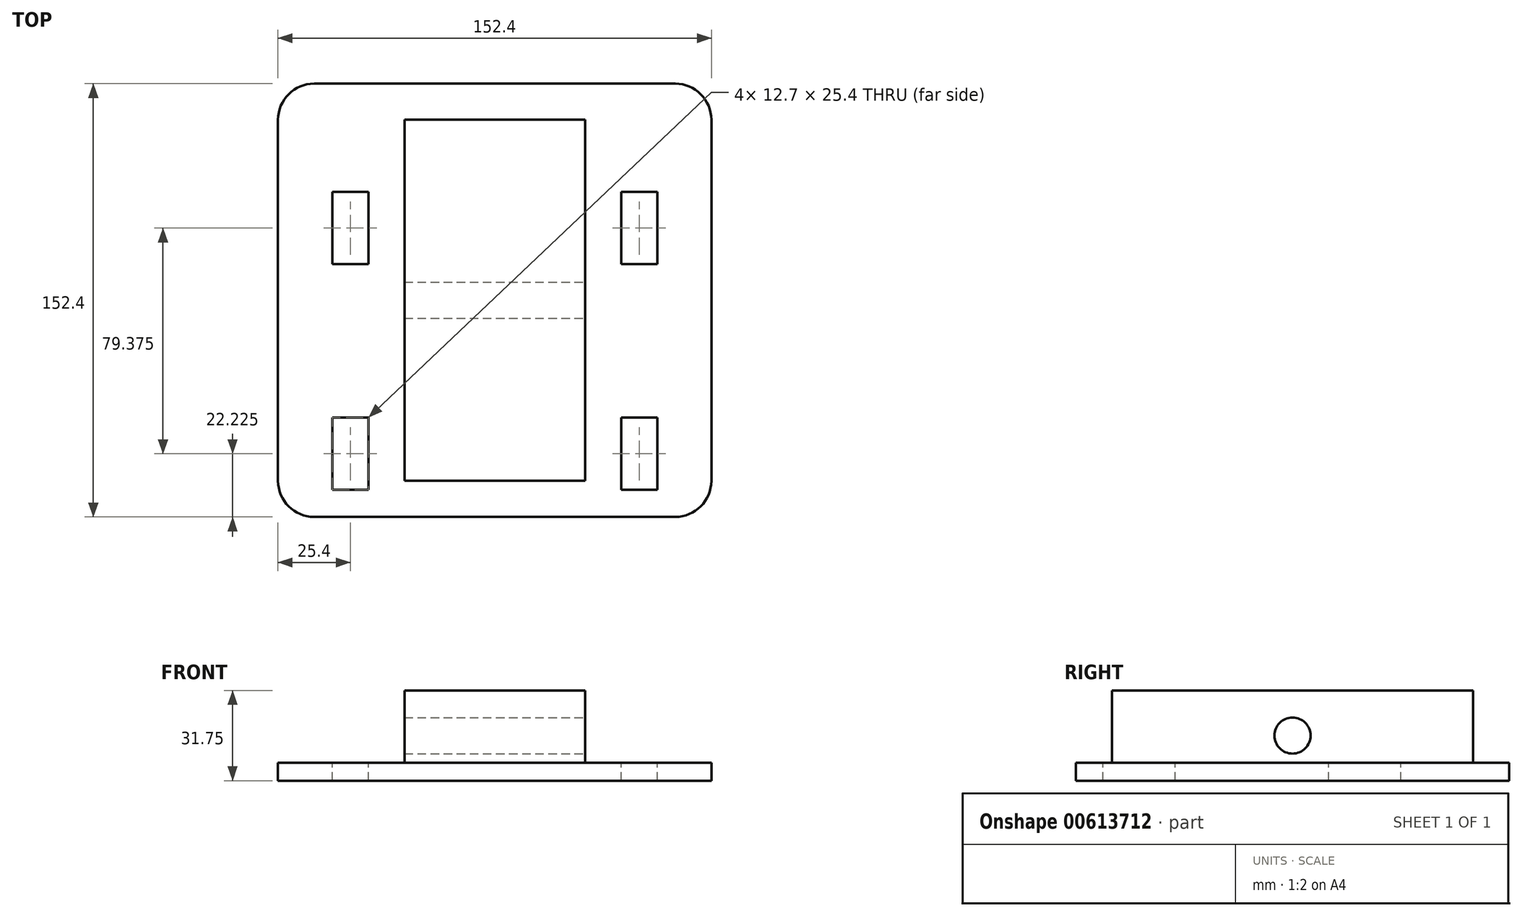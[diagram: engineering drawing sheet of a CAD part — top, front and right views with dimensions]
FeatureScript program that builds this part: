
annotation { "Feature Type Name" : "Feature", "Feature Type Description" : "" }
export const myFeature = defineFeature(function(context is Context, id is Id, definition is map)
    precondition{}
    {
        {
            var Q0;
            Q0=qCreatedBy(makeId("Top.planeOp"),FACE);
            var sketch = newSketch(context, id + "F0", { "sketchPlane" : qUnion([Q0])});
            skLineSegment(sketch, "E0.bottom", {"start": v(-63.5, 76.2) * mm, "end": v(63.5, 76.2) * mm});
            skLineSegment(sketch, "E0.top", {"start": v(-63.5, -76.2) * mm, "end": v(63.5, -76.2) * mm});
            skLineSegment(sketch, "E0.left", {"start": v(-76.2, 63.5) * mm, "end": v(-76.2, -63.5) * mm});
            skLineSegment(sketch, "E0.right", {"start": v(76.2, 63.5) * mm, "end": v(76.2, -63.5) * mm});
            skPoint(sketch, "E1.visualSharp", {"position": v(-76.2, 76.2) * mm});
            skArc(sketch, "E1.filletArc", {"start": v(-63.5, 76.2) * mm, "mid": v(-72.48, 72.48) * mm, "end": v(-76.2, 63.5) * mm});
            skPoint(sketch, "E2.visualSharp", {"position": v(-76.2, -76.2) * mm});
            skArc(sketch, "E2.filletArc", {"start": v(-76.2, -63.5) * mm, "mid": v(-72.48, -72.48) * mm, "end": v(-63.5, -76.2) * mm});
            skPoint(sketch, "E3.visualSharp", {"position": v(76.2, 76.2) * mm});
            skArc(sketch, "E3.filletArc", {"start": v(76.2, 63.5) * mm, "mid": v(72.48, 72.48) * mm, "end": v(63.5, 76.2) * mm});
            skPoint(sketch, "E4.visualSharp", {"position": v(76.2, -76.2) * mm});
            skArc(sketch, "E4.filletArc", {"start": v(63.5, -76.2) * mm, "mid": v(72.48, -72.48) * mm, "end": v(76.2, -63.5) * mm});
            skLineSegment(sketch, "E5.bottom", {"start": v(-57.15, 69.85) * mm, "end": v(57.15, 69.85) * mm});
            skLineSegment(sketch, "E5.top", {"start": v(-57.15, -69.85) * mm, "end": v(57.15, -69.85) * mm});
            skLineSegment(sketch, "E5.left", {"start": v(-69.85, 57.15) * mm, "end": v(-69.85, -57.15) * mm});
            skLineSegment(sketch, "E5.right", {"start": v(69.85, 57.15) * mm, "end": v(69.85, -57.15) * mm});
            skPoint(sketch, "E6.visualSharp", {"position": v(-69.85, 69.85) * mm});
            skArc(sketch, "E6.filletArc", {"start": v(-57.15, 69.85) * mm, "mid": v(-66.13, 66.13) * mm, "end": v(-69.85, 57.15) * mm});
            skPoint(sketch, "E7.visualSharp", {"position": v(-69.85, -69.85) * mm});
            skArc(sketch, "E7.filletArc", {"start": v(-69.85, -57.15) * mm, "mid": v(-66.13, -66.13) * mm, "end": v(-57.15, -69.85) * mm});
            skPoint(sketch, "E8.visualSharp", {"position": v(69.85, 69.85) * mm});
            skArc(sketch, "E8.filletArc", {"start": v(69.85, 57.15) * mm, "mid": v(66.13, 66.13) * mm, "end": v(57.15, 69.85) * mm});
            skPoint(sketch, "E9.visualSharp", {"position": v(69.85, -69.85) * mm});
            skArc(sketch, "E9.filletArc", {"start": v(57.15, -69.85) * mm, "mid": v(66.13, -66.13) * mm, "end": v(69.85, -57.15) * mm});
            skCircle(sketch, "E10", {"center": v(0, 0) * mm, "radius": 69.85 * mm});
            skSolve(sketch);
        }
        {
            var Q0;
            Q0=sQuery(id+"F0.wireOp",EDGE,"E0.bottom");
            var Q1;
            Q1=sQuery(id+"F0.wireOp",EDGE,"E1.filletArc");
            var Q2;
            Q2=sQuery(id+"F0.wireOp",EDGE,"E0.left");
            var Q3;
            Q3=sQuery(id+"F0.wireOp",EDGE,"E2.filletArc");
            var Q4;
            Q4=sQuery(id+"F0.wireOp",EDGE,"E0.top");
            var Q5;
            Q5=sQuery(id+"F0.wireOp",EDGE,"E4.filletArc");
            var Q6;
            Q6=sQuery(id+"F0.wireOp",EDGE,"E0.right");
            var Q7;
            Q7=sQuery(id+"F0.wireOp",EDGE,"E3.filletArc");
            var Q8;
            Q8=sQuery(id+"F0.wireOp",EDGE,"E5.bottom");
            var Q9;
            Q9=sQuery(id+"F0.wireOp",EDGE,"E6.filletArc");
            var Q10;
            Q10=sQuery(id+"F0.wireOp",EDGE,"E5.left");
            var Q11;
            Q11=sQuery(id+"F0.wireOp",EDGE,"E5.top");
            var Q12;
            Q12=sQuery(id+"F0.wireOp",EDGE,"E7.filletArc");
            var Q13;
            Q13=sQuery(id+"F0.wireOp",EDGE,"E5.right");
            var Q14;
            Q14=sQuery(id+"F0.wireOp",EDGE,"E8.filletArc");
            var Q15;
            Q15=sQuery(id+"F0.wireOp",EDGE,"E9.filletArc");
            extrude(context, id + "F1", {"bodyType" : ToolBodyType.SURFACE, "surfaceEntities" : qUnion([Q0, Q1, Q2, Q3, Q4, Q5, Q6, Q7, Q8, Q9, Q10, Q11, Q12, Q13, Q14, Q15]), "oppositeDirection" : true, "depth" : 50.8 * mm, "offsetDistance" : 25.4 * mm});
        }
        {
            var Q0;
            {var subQ0=sQuery(id+"F0.wireOp",EDGE,"E8.filletArc");Q0=makeQuery(id+"F0.imprint","IMPRINT",FACE,{"disambiguationData":[TD([[makeQuery(id+"F0.imprint","IMPRINT",EDGE,{"derivedFrom":subQ0}),1.0]])]});}
            var Q1;
            {var subQ0=sQuery(id+"F0.wireOp",EDGE,"E10");var subQ1=makeQuery(id+"F0.imprint","INTERSECT",VERTEX,{"derivedFrom":[sQuery(id+"F0.wireOp",EDGE,"E5.bottom"),subQ0]});Q1=makeQuery(id+"F0.imprint","IMPRINT",FACE,{"disambiguationData":[TD([[makeQuery(id+"F0.imprint","IMPRINT",EDGE,{"disambiguationData":[TD([[subQ1,1.0]])],"derivedFrom":subQ0}),1.0]])]});}
            var Q2;
            {var subQ0=sQuery(id+"F0.wireOp",EDGE,"E6.filletArc");Q2=makeQuery(id+"F0.imprint","IMPRINT",FACE,{"disambiguationData":[TD([[makeQuery(id+"F0.imprint","IMPRINT",EDGE,{"derivedFrom":subQ0}),1.0]])]});}
            var Q3;
            {var subQ0=sQuery(id+"F0.wireOp",EDGE,"E9.filletArc");Q3=makeQuery(id+"F0.imprint","IMPRINT",FACE,{"disambiguationData":[TD([[makeQuery(id+"F0.imprint","IMPRINT",EDGE,{"derivedFrom":subQ0}),1.0]])]});}
            var Q4;
            {var subQ0=sQuery(id+"F0.wireOp",EDGE,"E7.filletArc");Q4=makeQuery(id+"F0.imprint","IMPRINT",FACE,{"disambiguationData":[TD([[makeQuery(id+"F0.imprint","IMPRINT",EDGE,{"derivedFrom":subQ0}),1.0]])]});}
            var Q5;
            Q5=makeQuery(id+"F0.imprint","IMPRINT",FACE,{"disambiguationData":[TD([[makeQuery(id+"F0.imprint","IMPRINT",EDGE,{"derivedFrom":sQuery(id+"F0.wireOp",EDGE,"E0.bottom")}),-1.0]])]});
            extrude(context, id + "F2", {"entities" : qUnion([Q0, Q1, Q2, Q3, Q4, Q5]), "depth" : 6.35 * mm, "offsetDistance" : 25.4 * mm});
        }
        {
            var Q0;
            Q0=makeQuery(id+"F2.opExtrude","CAP_FACE",FACE,{"disambiguationData":[OSD([sQuery(id+"F0.wireOp",EDGE,"E0.bottom"),sQuery(id+"F0.wireOp",EDGE,"E0.top"),sQuery(id+"F0.wireOp",EDGE,"E0.left"),sQuery(id+"F0.wireOp",EDGE,"E0.right"),sQuery(id+"F0.wireOp",EDGE,"E1.filletArc"),sQuery(id+"F0.wireOp",EDGE,"E2.filletArc"),sQuery(id+"F0.wireOp",EDGE,"E3.filletArc"),sQuery(id+"F0.wireOp",EDGE,"E4.filletArc")])],"isStart":false});
            var sketch = newSketch(context, id + "F3", { "sketchPlane" : qUnion([Q0])});
            skLineSegment(sketch, "E11.bottom", {"start": v(-31.75, 63.5) * mm, "end": v(31.75, 63.5) * mm});
            skLineSegment(sketch, "E11.top", {"start": v(-31.75, -63.5) * mm, "end": v(31.75, -63.5) * mm});
            skLineSegment(sketch, "E11.left", {"start": v(-31.75, 63.5) * mm, "end": v(-31.75, -63.5) * mm});
            skLineSegment(sketch, "E11.right", {"start": v(31.75, 63.5) * mm, "end": v(31.75, -63.5) * mm});
            skSolve(sketch);
        }
        {
            var Q0;
            Q0=makeQuery(id+"F3.imprint","IMPRINT",FACE,{"disambiguationData":[TD([[makeQuery(id+"F3.imprint","IMPRINT",EDGE,{"derivedFrom":sQuery(id+"F3.wireOp",EDGE,"E11.bottom")}),-1.0]])]});
            extrude(context, id + "F4", {"entities" : qUnion([Q0]), "operationType" : NewBodyOperationType.ADD, "depth" : 25.4 * mm, "offsetDistance" : 25.4 * mm});
        }
        {
            var Q0;
            Q0=makeQuery(id+"F4.opExtrude","SWEPT_FACE",FACE,{"disambiguationData":[OSD([sQuery(id+"F3.wireOp",EDGE,"E11.right")])]});
            var sketch = newSketch(context, id + "F5", { "sketchPlane" : qUnion([Q0])});
            skCircle(sketch, "E12", {"center": v(0, 15.88) * mm, "radius": 6.35 * mm});
            skSolve(sketch);
        }
        {
            var Q0;
            Q0=makeQuery(id+"F5.imprint","IMPRINT",FACE,{"disambiguationData":[TD([[makeQuery(id+"F5.imprint","IMPRINT",EDGE,{"derivedFrom":sQuery(id+"F5.wireOp",EDGE,"E12")}),1.0]])]});
            extrude(context, id + "F6", {"entities" : qUnion([Q0]), "operationType" : NewBodyOperationType.REMOVE, "oppositeDirection" : true, "depth" : 63.5 * mm, "offsetDistance" : 25.4 * mm});
        }
        {
            var Q0;
            Q0=makeQuery(id+"F2.opExtrude","CAP_FACE",FACE,{"disambiguationData":[OSD([sQuery(id+"F0.wireOp",EDGE,"E0.bottom"),sQuery(id+"F0.wireOp",EDGE,"E0.top"),sQuery(id+"F0.wireOp",EDGE,"E0.left"),sQuery(id+"F0.wireOp",EDGE,"E0.right"),sQuery(id+"F0.wireOp",EDGE,"E1.filletArc"),sQuery(id+"F0.wireOp",EDGE,"E2.filletArc"),sQuery(id+"F0.wireOp",EDGE,"E3.filletArc"),sQuery(id+"F0.wireOp",EDGE,"E4.filletArc")])],"isStart":false});
            var sketch = newSketch(context, id + "F7", { "sketchPlane" : qUnion([Q0])});
            skLineSegment(sketch, "E13.bottom", {"start": v(-57.15, -41.28) * mm, "end": v(-44.45, -41.28) * mm});
            skLineSegment(sketch, "E13.top", {"start": v(-57.15, -66.68) * mm, "end": v(-44.45, -66.68) * mm});
            skLineSegment(sketch, "E13.left", {"start": v(-57.15, -41.28) * mm, "end": v(-57.15, -66.68) * mm});
            skLineSegment(sketch, "E13.right", {"start": v(-44.45, -41.28) * mm, "end": v(-44.45, -66.68) * mm});
            skLineSegment(sketch, "E14.bottom", {"start": v(44.45, -66.68) * mm, "end": v(57.15, -66.68) * mm});
            skLineSegment(sketch, "E14.top", {"start": v(44.45, -41.28) * mm, "end": v(57.15, -41.28) * mm});
            skLineSegment(sketch, "E14.left", {"start": v(44.45, -66.67) * mm, "end": v(44.45, -41.27) * mm});
            skLineSegment(sketch, "E14.right", {"start": v(57.15, -66.67) * mm, "end": v(57.15, -41.27) * mm});
            skLineSegment(sketch, "E15.bottom", {"start": v(-44.45, 12.7) * mm, "end": v(-57.15, 12.7) * mm});
            skLineSegment(sketch, "E15.top", {"start": v(-44.45, 38.1) * mm, "end": v(-57.15, 38.1) * mm});
            skLineSegment(sketch, "E15.left", {"start": v(-44.45, 12.7) * mm, "end": v(-44.45, 38.1) * mm});
            skLineSegment(sketch, "E15.right", {"start": v(-57.15, 12.7) * mm, "end": v(-57.15, 38.1) * mm});
            skLineSegment(sketch, "E16.bottom", {"start": v(44.45, 12.7) * mm, "end": v(57.15, 12.7) * mm});
            skLineSegment(sketch, "E16.top", {"start": v(44.45, 38.1) * mm, "end": v(57.15, 38.1) * mm});
            skLineSegment(sketch, "E16.left", {"start": v(44.45, 12.7) * mm, "end": v(44.45, 38.1) * mm});
            skLineSegment(sketch, "E16.right", {"start": v(57.15, 12.7) * mm, "end": v(57.15, 38.1) * mm});
            skSolve(sketch);
        }
        {
            var Q0;
            Q0=makeQuery(id+"F7.imprint","IMPRINT",FACE,{"disambiguationData":[TD([[makeQuery(id+"F7.imprint","IMPRINT",EDGE,{"derivedFrom":sQuery(id+"F7.wireOp",EDGE,"E16.bottom")}),1.0]])]});
            var Q1;
            Q1=makeQuery(id+"F7.imprint","IMPRINT",FACE,{"disambiguationData":[TD([[makeQuery(id+"F7.imprint","IMPRINT",EDGE,{"derivedFrom":sQuery(id+"F7.wireOp",EDGE,"E15.bottom")}),-1.0]])]});
            var Q2;
            Q2=makeQuery(id+"F7.imprint","IMPRINT",FACE,{"disambiguationData":[TD([[makeQuery(id+"F7.imprint","IMPRINT",EDGE,{"derivedFrom":sQuery(id+"F7.wireOp",EDGE,"E13.bottom")}),-1.0]])]});
            var Q3;
            Q3=makeQuery(id+"F7.imprint","IMPRINT",FACE,{"disambiguationData":[TD([[makeQuery(id+"F7.imprint","IMPRINT",EDGE,{"derivedFrom":sQuery(id+"F7.wireOp",EDGE,"E14.bottom")}),1.0]])]});
            extrude(context, id + "F8", {"entities" : qUnion([Q0, Q1, Q2, Q3]), "operationType" : NewBodyOperationType.REMOVE, "oppositeDirection" : true, "depth" : 6.35 * mm, "offsetDistance" : 25.4 * mm});
        }
    });
